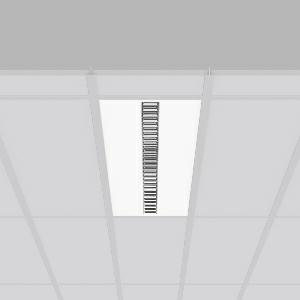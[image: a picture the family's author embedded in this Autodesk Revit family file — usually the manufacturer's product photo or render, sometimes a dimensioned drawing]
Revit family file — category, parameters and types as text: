
# Revit family: sonis_901679_002_1_8710
name_source: partatom
category: Lighting Fixtures
units: mm (PartAtom-declared; Revit-internal decimal feet)

## family parameters
Cut with Voids When Loaded = No
Host = Face
Light Source = No
Part Type = Normal
Room Calculation Point = No
Round Connector Dimension = Use Diameter
Shared = No

## types (1)
- SONIS (1 x LED Modul 840, 3450 lm, 4000)
    Apparent Load = 26 VA
    CIE Flux Codes = 82 100 100 100 100
    Color Rendering = 80
    Color Temperature = 4000
    Default Elevation = 1800 mm
    Description = Series: SONIS
High-efficiency lay-in luminaire for ceiling systems with visible mounting rails. Housing: metal, powder-coated. Alea optical system: Reflector structure (ABS, Aluminium-coated, highly polished) with integrated diffuser made of non-yellowing plastic (PMMA) opal for glare-free light at the workstation. Narrow beam, brilliant luminous effect. Suitable for Recessed ceiling mounting. Driver integrated. Perfect for office areas (RUG < 19) and environments with computer screens in accordance with EN 12464-1. 
Colour: white
Length: 1197 mm
Width: 297 mm
Cut-out length: 1175 mm
Cut-out width: 275 mm
Recess height: 27 mm
Lamp: LED
Socket: without socket
Colour temperature: 4000K
Colour rendering index (CRI): 80
System power: 26 W
Rated luminous flux: 3450 lm
Luminous efficiency: 133 lm/W
Control gear: Regulated power supply
Protection class: I
Type of protection: IP 20
    Height = 0 mm  [stored 0 ft]
    Lamp = 1 x LED Modul 840
    Lamp Light Flux = 3450 lm
    Lamp count = 1
    Length = 1197 mm
    Lifetime = 50000 h
    Luminous efficacy = 133 lm/W
    Manufacturer = RZB
    ModVariant = No
    Model = 901679.002.1
    Mounting Place = Ceiling
    Mounting Type = Recessed
    Number of Poles = 1
    OnlyDefault = Yes
    Power Factor = 1
    Product Name = SONIS
    Product group = Recessed modular luminaires
    ProductGroupID = 406
    Protection Class = Protection class I
    Protection Degree = IP 20
    RLX_Detail_Level = 1
    RLX_Emergency_Light_Flux = 0 lm
    RLX_Emergency_Type = 0
    RLX_Emergency_Type_DB = No
    RlxData = <blob elided: 34577 chars, md5=ebcef158>
    Socket = socket
    Standby Power = 0 W
    System Light Flux = 3450 lm
    System Power = 26 W
    Type Comments = Product without accessories
    Type Image = 901622.002.jpg
    URL = http://relux.com
    VarID = ---
    Voltage = 230 V
    Voltage Range = 220-240 V
    Weight = 0.00 kg
    Width = 297 mm

note: [stored X ft] marks values corroborated as IEEE doubles in the binary element streams (Revit-internal decimal feet)

## geometry (parser evidence)
native form markers: Blend x4, Sweep x9
no freeform markers — native parametric forms only
